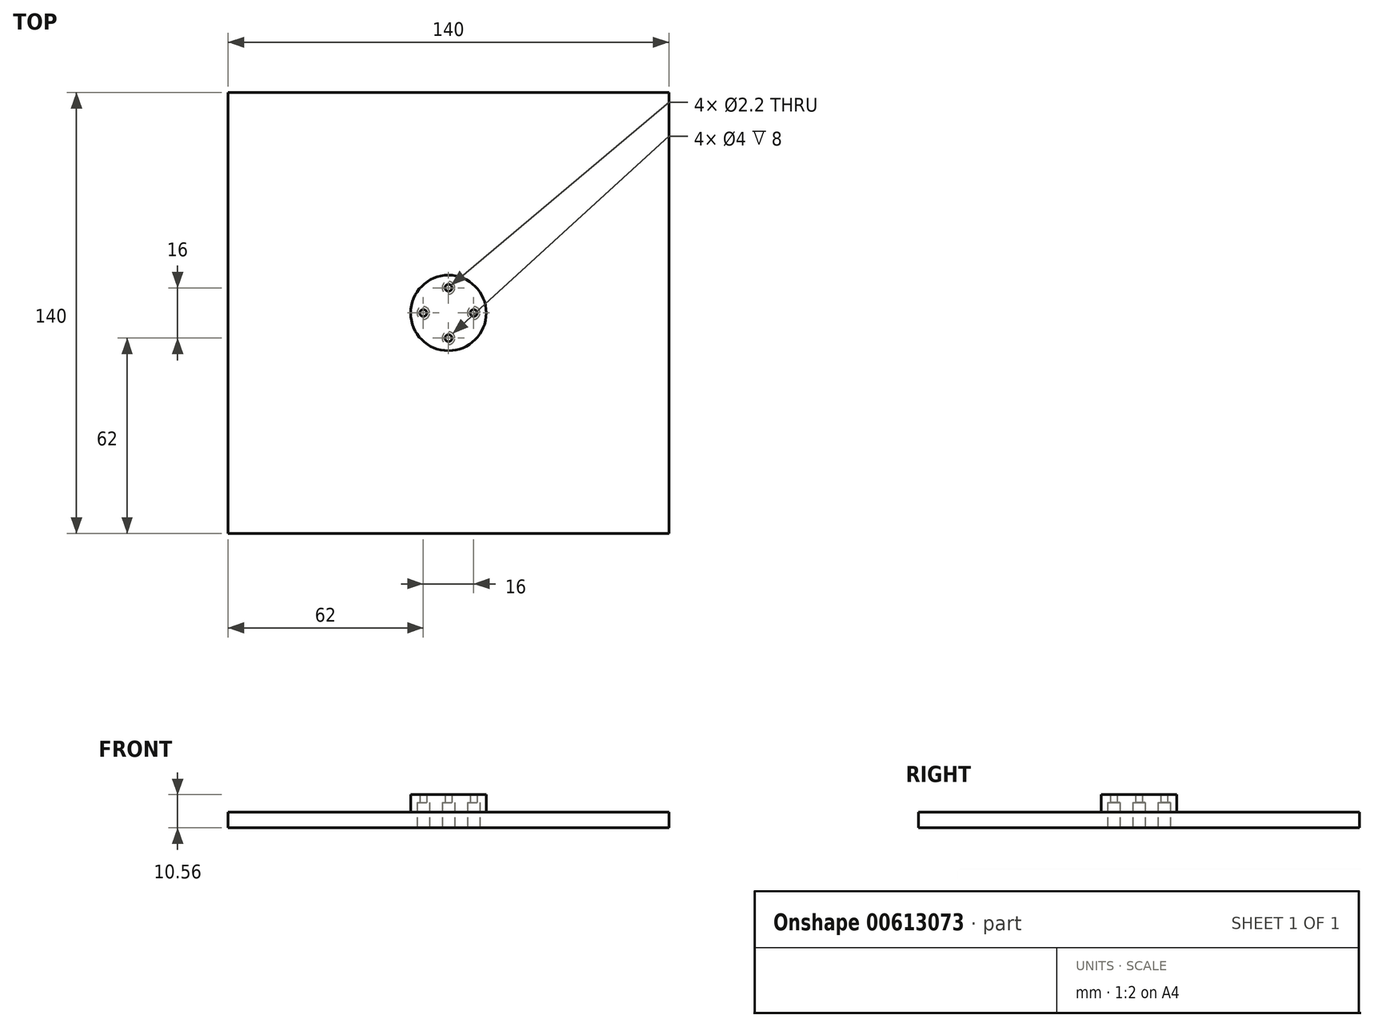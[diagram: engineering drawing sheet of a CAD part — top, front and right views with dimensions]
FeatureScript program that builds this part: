
annotation { "Feature Type Name" : "Feature", "Feature Type Description" : "" }
export const myFeature = defineFeature(function(context is Context, id is Id, definition is map)
    precondition{}
    {
        {
            var Q0;
            Q0=qCreatedBy(makeId("Top.planeOp"),FACE);
            var sketch = newSketch(context, id + "F0", { "sketchPlane" : qUnion([Q0])});
            skLineSegment(sketch, "E0.bottom", {"start": v(70, -70) * mm, "end": v(-70, -70) * mm});
            skLineSegment(sketch, "E0.top", {"start": v(70, 70) * mm, "end": v(-70, 70) * mm});
            skLineSegment(sketch, "E0.left", {"start": v(70, -70) * mm, "end": v(70, 70) * mm});
            skLineSegment(sketch, "E0.right", {"start": v(-70, -70) * mm, "end": v(-70, 70) * mm});
            skPoint(sketch, "E0.middle", {"position": v(0, 0) * mm});
            skCircle(sketch, "E1", {"center": v(0, 0) * mm, "radius": 8 * mm, "construction": true});
            skCircle(sketch, "E2", {"center": v(0, 0) * mm, "radius": 12 * mm});
            skPoint(sketch, "E3", {"position": v(0, 8) * mm});
            skPoint(sketch, "E4", {"position": v(8, 0) * mm});
            skPoint(sketch, "E5", {"position": v(0, -8) * mm});
            skPoint(sketch, "E6", {"position": v(-8, 0) * mm});
            skSolve(sketch);
        }
        {
            var Q0;
            Q0=qSketchRegion(id+"F0",true);
            extrude(context, id + "F1", {"entities" : qUnion([Q0]), "depth" : 5 * mm, "offsetDistance" : 25 * mm});
        }
        {
            var Q0;
            Q0=makeQuery(id+"F0.imprint","IMPRINT",FACE,{"disambiguationData":[TD([[makeQuery(id+"F0.imprint","IMPRINT",EDGE,{"derivedFrom":sQuery(id+"F0.wireOp",EDGE,"mxtSTHb5-2sSW-HKk8-hwSK-mRPs5wV7HEU5")}),-1.0]])]});
            var Q1;
            Q1=makeQuery(id+"F0.imprint","IMPRINT",FACE,{"disambiguationData":[TD([[makeQuery(id+"F0.imprint","IMPRINT",EDGE,{"derivedFrom":sQuery(id+"F0.wireOp",EDGE,"E2")}),1.0]])]});
            extrude(context, id + "F2", {"entities" : qUnion([Q0, Q1]), "operationType" : NewBodyOperationType.ADD, "depth" : 10.56 * mm, "offsetDistance" : 25 * mm});
        }
        {
            var Q0;
            Q0=sQuery(id+"F0.wireOp",VERTEX,"E4");
            var Q1;
            Q1=sQuery(id+"F0.wireOp",VERTEX,"E3");
            var Q2;
            Q2=sQuery(id+"F0.wireOp",VERTEX,"E6");
            var Q3;
            Q3=sQuery(id+"F0.wireOp",VERTEX,"E5");
            var Q4;
            Q4=makeQuery(id+"F1.opExtrude","SWEPT_BODY",BODY,{"disambiguationData":[OSD([sQuery(id+"F0.wireOp",EDGE,"E0.bottom"),sQuery(id+"F0.wireOp",EDGE,"E0.top"),sQuery(id+"F0.wireOp",EDGE,"E0.left"),sQuery(id+"F0.wireOp",EDGE,"E0.right"),sQuery(id+"F0.wireOp",EDGE,"E2")])]});
            hole(context, id + "F3", {"style" : HoleStyle.C_BORE, "endStyle" : HoleEndStyle.BLIND, "oppositeDirection" : true, "holeDiameter" : 2.2 * mm, "cBoreDiameter" : 4 * mm, "cBoreDepth" : 8 * mm, "majorDiameter" : 5 * mm, "holeDepth" : 12 * mm, "isTappedThrough" : true, "tappedDepth" : 12 * mm, "tapClearance" : 3, "locations" : qUnion([Q0, Q1, Q2, Q3]), "scope" : qUnion([Q4])});
        }
    });
